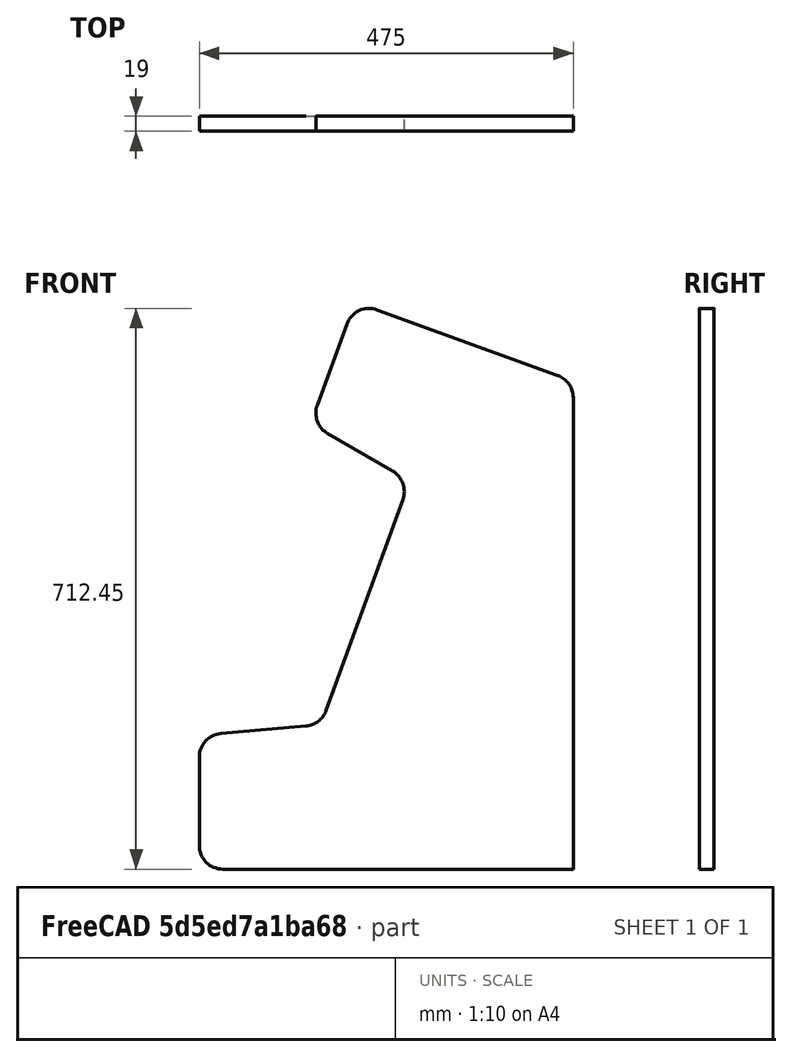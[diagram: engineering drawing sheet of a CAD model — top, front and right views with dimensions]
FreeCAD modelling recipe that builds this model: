
FCSTD DOCUMENT  (FreeCAD 0.18R16131 (Git))
Label: 9000_ASM_Profile_Sidewall
License: All rights reserved
LicenseURL: http://en.wikipedia.org/wiki/All_rights_reserved
objects: TechDraw::DrawViewDimension×11, Sketcher::SketchObject×2, Spreadsheet::Sheet×1, PartDesign::Pad×1, PartDesign::Fillet×1, PartDesign::Body×1, TechDraw::DrawSVGTemplate×1, TechDraw::DrawViewPart×1, TechDraw::DrawPage×1
note: 6 computed .brp shape members not serialized (recipe doc carries the construction recipe); baked Part::Feature solids carry a one-line shape summary decoded from their .brp

FEATURE [Spreadsheet::Sheet] Spreadsheet  label="XLS"
  cells = B2=BODY FLOOR; E2=Ext.Ref; B3=Z=; C3=16; D3=.T; E3=Thichness; B4=Y=; C4=500; D4=.W; E4=Width; B5=X=; C5=400; D5=.D; E5=Depth; B7=Position Side Wall; D8=Left; E8=Right; B9=X0; D9(X0)==+C5; B10=Y0; C10=Y0_2; D10(Y0)==+C4; E10(Y0_2)==+D10 - D11; B11=Z0; D11(Z0)=13; B15=Position Front Wall; B16=x; C16=X0_Front; D16(X0_Front)==+H16 * abs(cos(D19)); F16=Distance on incline; G16=nS; H16(nS)=50; I16=mm; B17=y; C17=Y0_Front; D17(Y0_Front)=0; B18=z; C18=Z0_Front; D18(Z0_Front)==+H16 * abs(sin(D19)) + H18 + H20; F18=Hight of Incline; G18=nH; H18(nH)==125 + 2; I18=mm; B19=angle; C19=angley; D19(angley)=-70; F20=Thickness Material; H20=13; B22=Position Pedastil; B23=x; C23=x_pedastil; D23(x_pedastil)=0; B24=y; C24=y_pedastil; D24(y_pedastil)=0; B25=z; C25=z_pedastil; D25(z_pedastil)=-716; B27=Position Marquee; B28=x; C28==x_pedastil; B29=y; C29==y_pedastil; B30=z; C30==z_pedastil; B31=Incline
FEATURE [Sketcher::SketchObject] Sketch
  Placement = pos=(0,0,0) rot=(1,0,0;1.5708rad)
  sketch-geometry (8):
    g0: LineSegment StartX=-18.8859 StartY=-15 StartZ=0 EndX=416.114 EndY=-15 EndZ=0
    g1: LineSegment StartX=416.114 StartY=-15 StartZ=0 EndX=416.114 EndY=575 EndZ=0
    g2: LineSegment StartX=416.114 StartY=575 StartZ=0 EndX=176.973 EndY=663.523 EndZ=0
    g3: LineSegment StartX=176.973 StartY=663.523 StartZ=0 EndX=130.145 EndY=542.25 EndZ=0
    g4: LineSegment StartX=130.145 StartY=542.25 StartZ=0 EndX=271.305 EndY=491.516 EndZ=0
    g5: LineSegment StartX=271.305 StartY=491.516 StartZ=0 EndX=134.264 EndY=115 EndZ=0
    g6: LineSegment StartX=134.264 StartY=115 StartZ=0 EndX=-18.8859 EndY=115 EndZ=0
    g7: LineSegment StartX=-18.8859 StartY=115 StartZ=0 EndX=-18.8859 EndY=-15 EndZ=0
  constraints (20):
    c: Coincident(g0,g1)
    c: Coincident(g1,g2)
    c: Coincident(g2,g3)
    c: Coincident(g3,g4)
    c: Coincident(g4,g5)
    c: Coincident(g5,g6)
    c: Coincident(g6,g7)
    c: Perpendicular(g6,g7)
    c: Vertical(g7)
    c: Angle(g5,g6) = 1.91986
    c: Vertical(g1)
    c: Distance(g2) = 255
    c: Distance(g4) = 150
    c: Distance(g3) = 130
    c: Coincident(g7,g0)
    c: Horizontal(g0)
    c: DistanceY(g7,g7) = 130
    c: Distance(g1) = 590
    c: DistanceX(g0,g0) = 435
    c: DistanceY(g0,g-1) = 15
FEATURE [Sketcher::SketchObject] Sketch001
  MapMode = 5
  Placement = pos=(0,0,0) rot=(1,0,0;1.5708rad)
  Support = -> [XZ_Plane]
  sketch-geometry (8):
    g0: LineSegment StartX=-39.6333 StartY=-30.0691 StartZ=0 EndX=-39.6333 EndY=139.931 EndZ=0
    g1: LineSegment StartX=-39.6333 StartY=139.931 StartZ=0 EndX=114.876 EndY=153.449 EndZ=0
    g2: LineSegment StartX=114.876 StartY=153.449 StartZ=0 EndX=227.584 EndY=463.112 EndZ=0
    g3: LineSegment StartX=227.584 StartY=463.112 StartZ=0 EndX=101.724 EndY=535.778 EndZ=0
    g4: LineSegment StartX=101.724 StartY=535.778 StartZ=0 EndX=158.157 EndY=690.827 EndZ=0
    g5: LineSegment StartX=158.157 StartY=690.827 StartZ=0 EndX=435.367 EndY=589.931 EndZ=0
    g6: LineSegment StartX=435.367 StartY=589.931 StartZ=0 EndX=435.367 EndY=-30.0691 EndZ=0
    g7: LineSegment StartX=435.367 StartY=-30.0691 StartZ=0 EndX=-39.6333 EndY=-30.0691 EndZ=0
  constraints (21):
    c: Coincident(g0,g1)
    c: Coincident(g1,g2)
    c: Coincident(g2,g3)
    c: Coincident(g3,g4)
    c: Coincident(g4,g5)
    c: Coincident(g5,g6)
    c: Coincident(g6,g7)
    c: Coincident(g7,g0)
    c: Horizontal(g7)
    c: Vertical(g6)
    c: Vertical(g0)
    c: Perpendicular(g5,g4)
    c: Angle(g7,g2) = 1.22173
    c: Angle(g5,g6) = 1.91986
    c: DistanceY(g6,g6) = 620
    c: DistanceX(g7,g7) = 475
    c: DistanceY(g0,g0) = 170
    c: Distance(g5) = 295
    c: Distance(g4) = 165
    c: Angle(g3,g2) = 1.74533
    c: Angle(g0,g1) = 1.65806
FEATURE [PartDesign::Pad] Pad
  Length = 19
  Length2 = 100
  Placement = pos=(0,0,0) rot=(1,0,0;1.5708rad)
  Profile = -> Sketch001
  Reversed = true
  Type = 0
FEATURE [PartDesign::Fillet] Fillet
  Base = -> Pad [Edge1,Edge2,Edge11,Edge14,Edge17,Edge8,Edge5]
  BaseFeature = -> Pad
  Placement = pos=(0,0,0) rot=(1,0,0;1.5708rad)
  Radius = 30
FEATURE [PartDesign::Body] Body
  Group = -> [Sketch001,Pad,Fillet]
  Origin = -> Origin
  Tip = -> Fillet
FEATURE [TechDraw::DrawSVGTemplate] Template
  EditableTexts = Designed_by_Name=Designed by Name; Drawing_number=Drawing number; FC-Date=Date; FC-SC=Scale; FC-SH=Sheet; FC-Title=Title; Subtitle=Subtitle; Weight=Weight
  Height = 210
  Orientation = 1
  Width = 297
FEATURE [TechDraw::DrawViewPart] View
  CoarseView = false
  Direction = (0,1,0)
  Focus = 100
  HardHidden = false
  IsoCount = 0
  IsoHidden = true
  IsoVisible = true
  LockPosition = false
  Perspective = false
  Rotation = -90
  Scale = 0.2
  ScaleType = 0
  SeamHidden = false
  SeamVisible = false
  SmoothHidden = false
  SmoothVisible = false
  Source = -> [Fillet,Sketch001]
  X = 128.3
  Y = 134.016
FEATURE [TechDraw::DrawViewDimension] Dimension
  Arbitrary = false
  FormatSpec = %.2f
  LockPosition = false
  MeasureType = 1
  OverTolerance = 0
  References2D = -> [View]
  Rotation = 0
  ScaleType = 0
  Type = 1
  UnderTolerance = 0
  X = 3.00512
  Y = -57.3431
FEATURE [TechDraw::DrawViewDimension] Dimension001
  Arbitrary = false
  FormatSpec = %.2f
  LockPosition = false
  MeasureType = 1
  OverTolerance = 0
  References2D = -> [View]
  Rotation = 0
  ScaleType = 0
  Type = 2
  UnderTolerance = 0
  X = 104.845
  Y = -5.10871
FEATURE [TechDraw::DrawViewDimension] Dimension002
  Arbitrary = false
  FormatSpec = %.2f
  LockPosition = false
  MeasureType = 1
  OverTolerance = 0
  References2D = -> [View]
  Rotation = 0
  ScaleType = 0
  Type = 1
  UnderTolerance = 0
  X = 52.8288
  Y = 60.5431
FEATURE [TechDraw::DrawViewDimension] Dimension003
  Arbitrary = false
  FormatSpec = %.2f
  LockPosition = false
  MeasureType = 1
  OverTolerance = 0
  References2D = -> [View]
  Rotation = 0
  ScaleType = 0
  Type = 0
  UnderTolerance = 0
  X = -63.7149
  Y = 24.8892
FEATURE [TechDraw::DrawViewDimension] Dimension004
  Arbitrary = false
  FormatSpec = %.2f
  LockPosition = false
  MeasureType = 1
  OverTolerance = 0
  References2D = -> [View]
  Rotation = 0
  ScaleType = 0
  Type = 6
  UnderTolerance = 0
  X = -49.7743
  Y = -26.9413
FEATURE [TechDraw::DrawViewDimension] Dimension005
  Arbitrary = false
  FormatSpec = %.2f
  LockPosition = false
  MeasureType = 1
  OverTolerance = 0
  References2D = -> [View]
  Rotation = 0
  ScaleType = 0
  Type = 6
  UnderTolerance = 0
  X = 51.5247
  Y = -30.3126
FEATURE [TechDraw::DrawViewDimension] Dimension006
  Arbitrary = false
  FormatSpec = %.2f
  LockPosition = false
  MeasureType = 1
  OverTolerance = 0
  References2D = -> [View]
  Rotation = 0
  ScaleType = 0
  Type = 2
  UnderTolerance = 0
  X = -92.8126
  Y = -16.2238
FEATURE [TechDraw::DrawViewDimension] Dimension007
  Arbitrary = false
  FormatSpec = %.2f
  LockPosition = false
  MeasureType = 1
  OverTolerance = 0
  References2D = -> [View]
  Rotation = 0
  ScaleType = 0
  Type = 2
  UnderTolerance = 0
  X = -34.1387
  Y = -17.5113
FEATURE [TechDraw::DrawViewDimension] Dimension008
  Arbitrary = false
  FormatSpec = %.2f
  LockPosition = false
  MeasureType = 1
  OverTolerance = 0
  References2D = -> [View]
  Rotation = 0
  ScaleType = 0
  Type = 1
  UnderTolerance = 0
  X = 31.6166
  Y = 8.92218
FEATURE [TechDraw::DrawViewDimension] Dimension009
  Arbitrary = false
  FormatSpec = %.2f
  LockPosition = false
  MeasureType = 1
  OverTolerance = 0
  References2D = -> [View]
  Rotation = 0
  ScaleType = 0
  Type = 1
  UnderTolerance = 0
  X = 50.5208
  Y = 31.5948
FEATURE [TechDraw::DrawViewDimension] Dimension010
  Arbitrary = false
  FormatSpec = %.2f
  LockPosition = false
  MeasureType = 1
  OverTolerance = 0
  References2D = -> [View]
  Rotation = 0
  ScaleType = 0
  Type = 2
  UnderTolerance = 0
  X = 16.7059
  Y = -8.94018
FEATURE [TechDraw::DrawPage] Page
  KeepUpdated = true
  ProjectionType = 0
  Template = -> Template
  Views = -> [View,Dimension,Dimension001,Dimension002,Dimension003,Dimension004,Dimension005,Dimension006,Dimension007,Dimension008,Dimension009,Dimension010]
